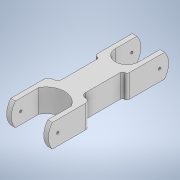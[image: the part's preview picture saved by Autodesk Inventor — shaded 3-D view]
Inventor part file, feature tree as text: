
AUTODESK INVENTOR PART (.ipt)
format: ipt  version: 2022 (Build 260153000, 153)  size: 208,384 bytes
history: native  units: mm
features: extrude x5, fillet x5, sketch x5
ambient origin geometry x8: Origin, YZ Plane, XZ Plane, XY Plane, X Axis, Y Axis, Z Axis, Center Point
bodies: Solid1 (feature_tree)
feature tree (15):
  extrude  "Extrusion1"  Depth=10.0mm
  extrude  "Extrusion2"  Depth=50.0mm TaperAngle=0.0deg
  fillet  "Fillet1"  Radius=10.0mm
  fillet  "Fillet2"  Radius=10.0mm
  fillet  "Fillet3"  Radius=10.0mm
  fillet  "Fillet4"  Radius=50.0mm
  fillet  "Fillet5"  Radius=10.0mm
  extrude  "Extrusion3"  Depth=10.0mm
  extrude  "Extrusion4"  Depth=5.0mm
  extrude  "Extrusion5"  Depth=5.0mm
  sketch  "Sketch1"  dims[d2=90.0mm d4=10.0mm]
  sketch  "Sketch2"  dims[d5=10.0mm d13=50.0mm d14=0.0mm d18=10.0mm d19=10.0mm d25=10.0mm d28=50.0mm d29=0.0mm d30=10.0mm]
  sketch  "Sketch3"  dims[d31=10.0mm d32=10.0mm]
  sketch  "Sketch4"  dims[d33=5.0mm d34=5.0mm]
  sketch  "Sketch5"  dims[d36=5.0mm d40=5.0mm d41=150.25mm d42=0.0mm d43=10.0mm d44=7.5mm d45=30.0mm d47=15.0mm d48=5.0mm d49=0.0mm d50=2.5mm d51=2.5mm d52=40.0mm d53=20.0mm d54=5.0mm d55=0.0mm d15=0.5mm d16=0.872665mm]
